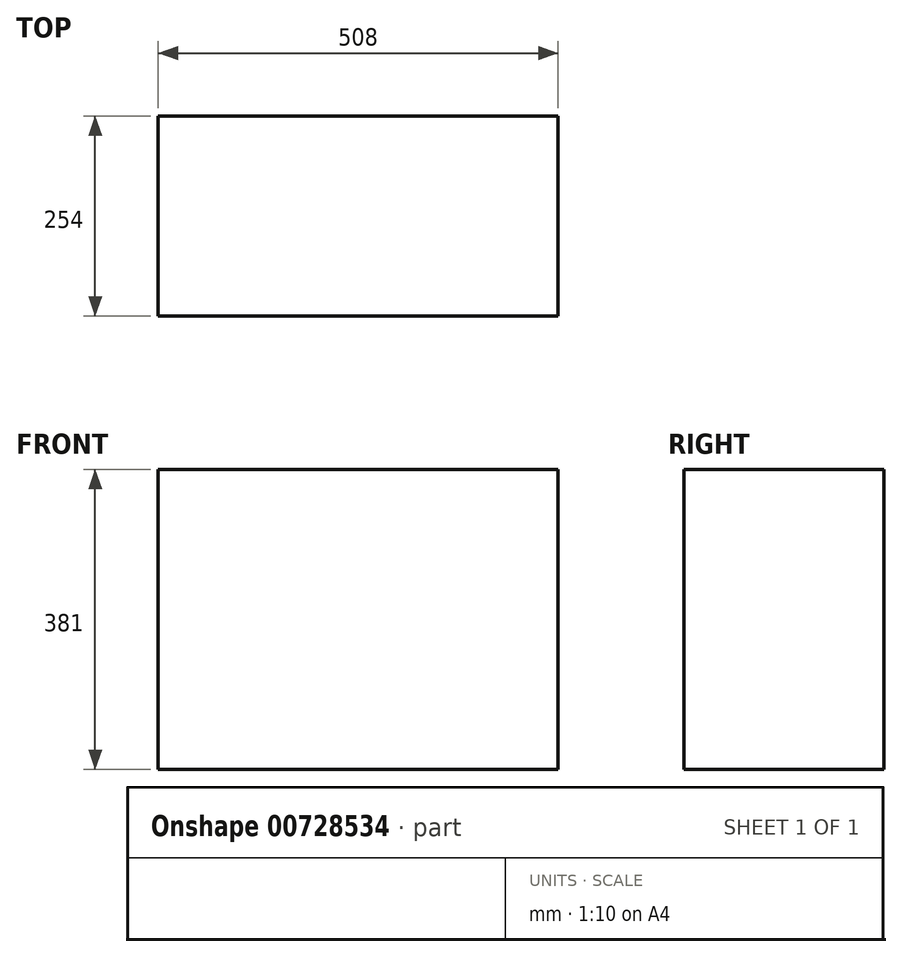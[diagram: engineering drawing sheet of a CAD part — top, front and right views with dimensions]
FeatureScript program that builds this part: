
annotation { "Feature Type Name" : "Feature", "Feature Type Description" : "" }
export const myFeature = defineFeature(function(context is Context, id is Id, definition is map)
    precondition{}
    {
        {
            var Q0;
            Q0=qCreatedBy(makeId("Top.planeOp"),FACE);
            var sketch = newSketch(context, id + "F0", { "sketchPlane" : qUnion([Q0])});
            skLineSegment(sketch, "E0.bottom", {"start": v(254, 127) * mm, "end": v(-254, 127) * mm});
            skLineSegment(sketch, "E0.top", {"start": v(254, -127) * mm, "end": v(-254, -127) * mm});
            skLineSegment(sketch, "E0.left", {"start": v(254, 127) * mm, "end": v(254, -127) * mm});
            skLineSegment(sketch, "E0.right", {"start": v(-254, 127) * mm, "end": v(-254, -127) * mm});
            skPoint(sketch, "E0.middle", {"position": v(0, 0) * mm});
            skSolve(sketch);
        }
        {
            var Q0;
            Q0 = qSketchRegion(id + "F0", true);
            extrude(context, id + "F1", {"entities" : qUnion([Q0]), "depth" : 381 * mm, "offsetDistance" : 25.4 * mm});
        }
    });
